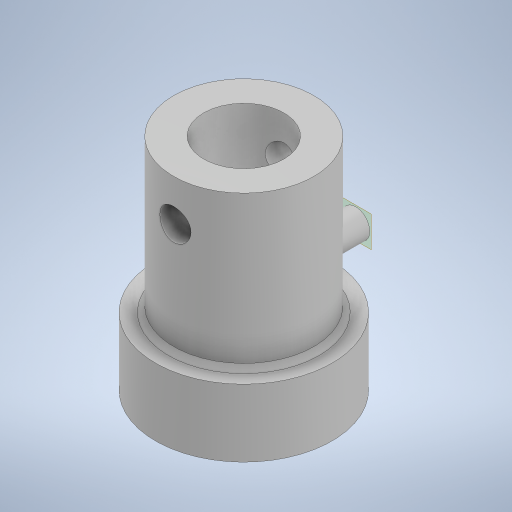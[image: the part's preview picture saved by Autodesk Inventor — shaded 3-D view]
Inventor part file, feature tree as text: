
AUTODESK INVENTOR PART (.ipt)
format: ipt  version: 2023 (Build 270158030, 158C)  size: 438,784 bytes
history: mixed  units: in
note: dims shown in document units (in); Inventor stores cm internally (conversion verified against a paired STEP export)
features: other x6, plane x1, extrude x1, sketch x1, imported_body x1
ambient origin geometry x8: Origin, YZ Plane, XZ Plane, XY Plane, X Axis, Y Axis, Z Axis, Center Point
bodies: Solid1 (imported_parasolid), Solid4 (imported_parasolid), Solid6 (imported_parasolid), Solid10 (imported_parasolid), Solid23 (imported_parasolid), Solid37 (imported_parasolid)
feature tree (10):
  other  "MouseEarbar"
  plane  "Work Plane1"
  extrude  "Extrusion1"  Depth=0.1181in
  sketch  "Sketch1"  dims[d0=0.0in d1=0.1181in d2=0.1575in d3=0.1575in d4=0.0in]
  other  "Rat_ToothHolder"
  other  "Mouse_ToothHolder"
  other  "MouseNoseCone"
  other  "RatNoseCone"
  other  "RatEarbar_1"
  imported_body  NMx_Import_Brep_tag  [imported B-rep: ~5 faces, bbox_mm=None]
